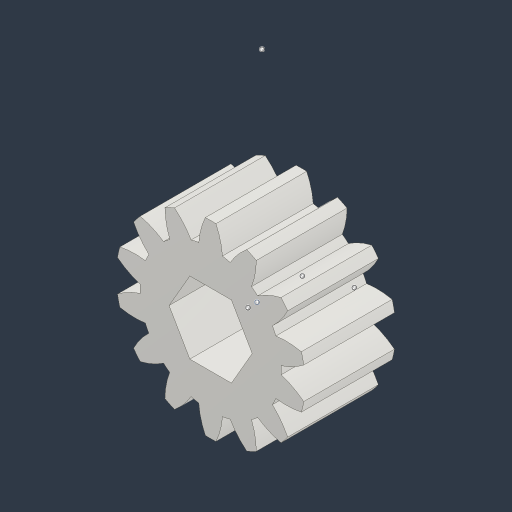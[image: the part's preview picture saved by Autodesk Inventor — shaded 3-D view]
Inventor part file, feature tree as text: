
AUTODESK INVENTOR PART (.ipt)
format: ipt  version: 2024.3 (Build 283343000, 343)  size: 208,896 bytes
history: native  units: mm (DEFAULTED — no unit token found)
features: plane x3, other x3, extrude x2, sketch x2
ambient origin geometry x8: Origin, YZ Plane, XZ Plane, XY Plane, X Axis, Y Axis, Z Axis, Center Point
bodies: Solid1 (feature_tree)
feature tree (10):
  extrude  "Extrusion1"  Depth=16.0mm TaperAngle=0.0deg
  plane  "Work Plane2"
  plane  "Work Plane8"
  plane  "Work Plane9"
  other  "Spur Gear"
  extrude  "Extrusion2"  Depth=10.0mm TaperAngle=0.0deg
  sketch  "Sketch1"  dims[d0=33.307842mm d1=16.0mm d2=0.0mm]
  other  "Srf1"
  sketch  "Sketch3"  dims[d3=28.0mm d4=10.0mm d5=0.0mm d16=29.6mm d17=0.0mm d34=2.243995mm d39=0.0mm d41=0.0mm d43=29.6mm d46=29.6mm d47=0.0mm d48=0.0mm d49=12.7mm d50=0.0mm d51=0.0mm]
  other  "Pitch Diameter"
